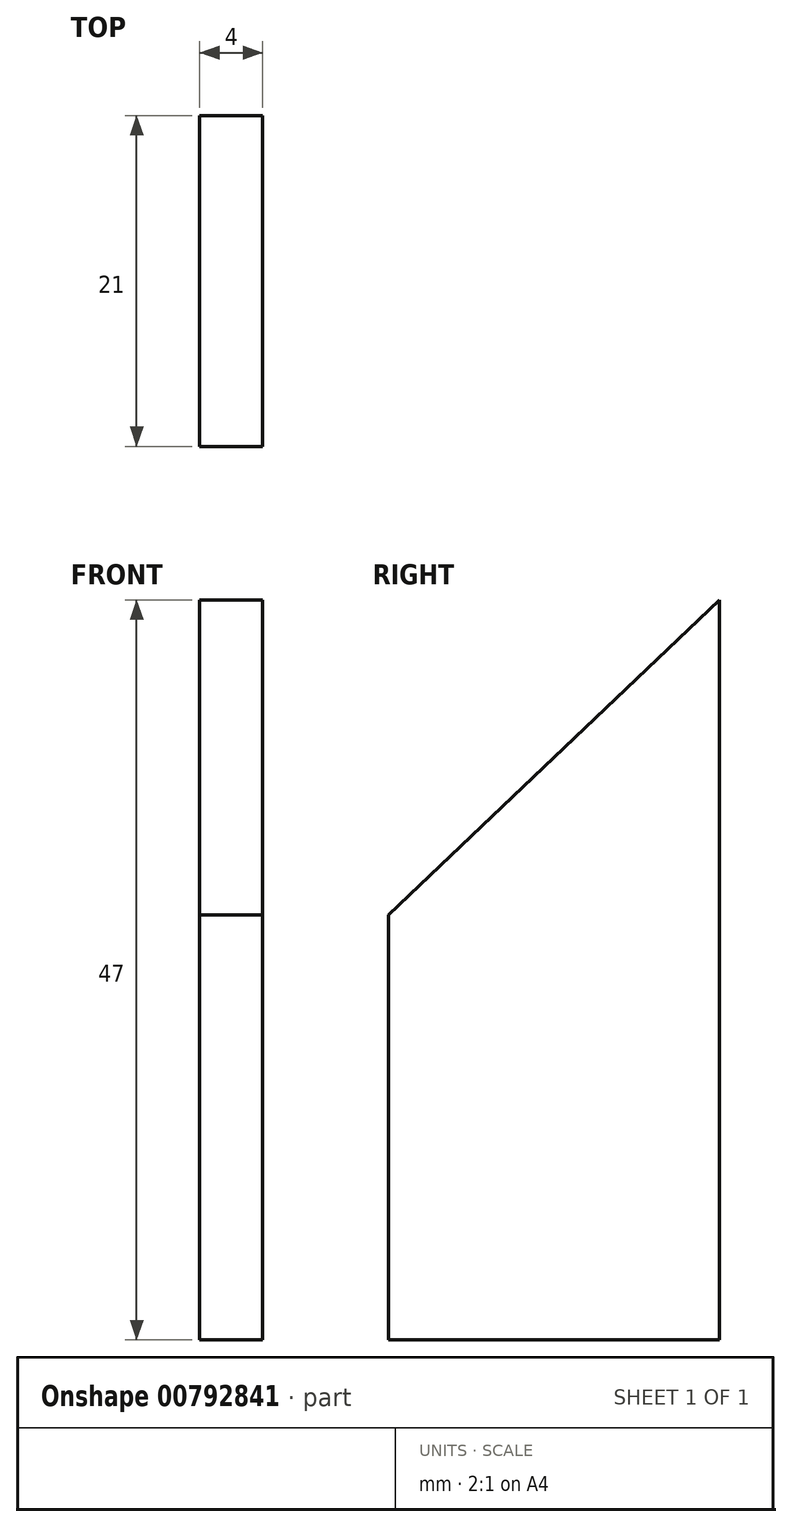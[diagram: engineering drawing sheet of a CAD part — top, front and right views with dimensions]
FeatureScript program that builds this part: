
annotation { "Feature Type Name" : "Feature", "Feature Type Description" : "" }
export const myFeature = defineFeature(function(context is Context, id is Id, definition is map)
    precondition{}
    {
        {
            var Q0;
            Q0=qCreatedBy(makeId("Front.planeOp"),FACE);
            var sketch = newSketch(context, id + "F0", { "sketchPlane" : qUnion([Q0])});
            skLineSegment(sketch, "E0.bottom", {"start": v(2, 23.5) * mm, "end": v(-2, 23.5) * mm});
            skLineSegment(sketch, "E0.top", {"start": v(2, -23.5) * mm, "end": v(-2, -23.5) * mm});
            skLineSegment(sketch, "E0.left", {"start": v(2, 23.5) * mm, "end": v(2, -23.5) * mm});
            skLineSegment(sketch, "E0.right", {"start": v(-2, 23.5) * mm, "end": v(-2, -23.5) * mm});
            skPoint(sketch, "E0.middle", {"position": v(0, 0) * mm});
            skSolve(sketch);
        }
        {
            var Q0;
            Q0 = qSketchRegion(id + "F0", true);
            extrude(context, id + "F1", {"entities" : qUnion([Q0]), "depth" : 21 * mm, "offsetDistance" : 25 * mm});
        }
        {
            var Q0;
            Q0=makeQuery(id+"F1.opExtrude","CAP_EDGE",EDGE,{"disambiguationData":[OSD([sQuery(id+"F0.wireOp",EDGE,"E0.bottom")])],"isStart":false});
            chamfer(context, id + "F2", {"entities" : qUnion([Q0]), "chamferType" : ChamferType.TWO_OFFSETS, "width1" : 20 * mm, "oppositeDirection" : false, "width2" : 21 * mm, "tangentPropagation" : true});
        }
    });
